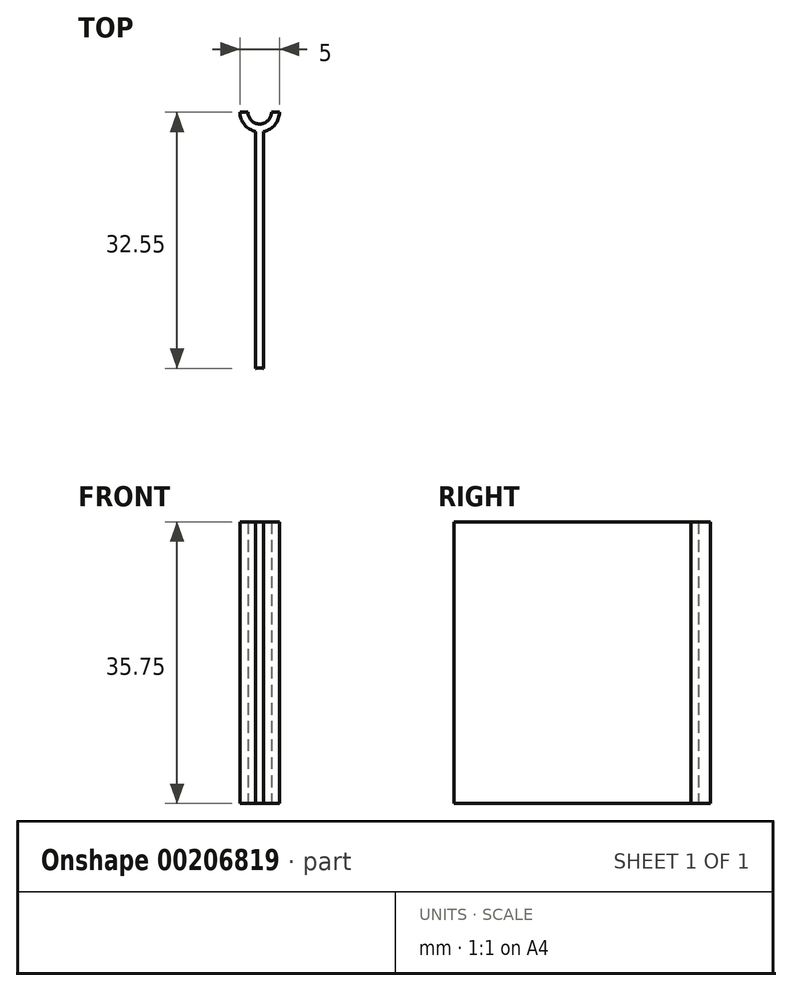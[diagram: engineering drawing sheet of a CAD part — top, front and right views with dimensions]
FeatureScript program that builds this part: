
annotation { "Feature Type Name" : "Feature", "Feature Type Description" : "" }
export const myFeature = defineFeature(function(context is Context, id is Id, definition is map)
    precondition{}
    {
        {
            var Q0;
            Q0=qCreatedBy(makeId("Top.planeOp"),FACE);
            var sketch = newSketch(context, id + "F0", { "sketchPlane" : qUnion([Q0])});
            skLineSegment(sketch, "E0.bottom", {"start": v(2.5, 17.5) * mm, "end": v(-2.5, 17.5) * mm, "construction": true});
            skLineSegment(sketch, "E0.top", {"start": v(2.5, -17.5) * mm, "end": v(-2.5, -17.5) * mm, "construction": true});
            skLineSegment(sketch, "E0.left", {"start": v(2.5, 17.5) * mm, "end": v(2.5, -17.5) * mm, "construction": true});
            skLineSegment(sketch, "E0.right", {"start": v(-2.5, 17.5) * mm, "end": v(-2.5, -17.5) * mm, "construction": true});
            skPoint(sketch, "E0.middle", {"position": v(0, 0) * mm});
            skLineSegment(sketch, "E1", {"start": v(0, 0) * mm, "end": v(0, 17.5) * mm});
            skLineSegment(sketch, "E2", {"start": v(0, 17.5) * mm, "end": v(0, -17.5) * mm, "construction": true});
            skLineSegment(sketch, "E3.left", {"start": v(-0.5, 15.05) * mm, "end": v(-0.5, -15.05) * mm});
            skLineSegment(sketch, "E3.right", {"start": v(0.5, 15.05) * mm, "end": v(0.5, -15.05) * mm});
            skArc(sketch, "E4", {"start": v(-2.5, 17.5) * mm, "mid": v(0, 15) * mm, "end": v(2.5, 17.5) * mm});
            skArc(sketch, "E5", {"start": v(-1.5, 17.5) * mm, "mid": v(0, 16) * mm, "end": v(1.5, 17.5) * mm});
            skLineSegment(sketch, "E6", {"start": v(-2.5, 17.5) * mm, "end": v(-1.5, 17.5) * mm});
            skLineSegment(sketch, "E7", {"start": v(1.5, 17.5) * mm, "end": v(2.5, 17.5) * mm});
            skArc(sketch, "E8", {"start": v(-2.5, -17.5) * mm, "mid": v(0, -15) * mm, "end": v(2.5, -17.5) * mm});
            skArc(sketch, "E9", {"start": v(-1.5, -17.5) * mm, "mid": v(0, -16) * mm, "end": v(1.5, -17.5) * mm});
            skLineSegment(sketch, "E10", {"start": v(-2.5, -17.5) * mm, "end": v(-1.5, -17.5) * mm});
            skLineSegment(sketch, "E11", {"start": v(1.5, -17.5) * mm, "end": v(2.5, -17.5) * mm});
            skSolve(sketch);
        }
        {
            var Q0;
            {var subQ0=sQuery(id+"F0.wireOp",EDGE,"E6");Q0=makeQuery(id+"F0.imprint","IMPRINT",FACE,{"disambiguationData":[TD([[makeQuery(id+"F0.imprint","IMPRINT",EDGE,{"derivedFrom":subQ0}),-1.0]])]});}
            var Q1;
            {var subQ0=sQuery(id+"F0.wireOp",EDGE,"E7");Q1=makeQuery(id+"F0.imprint","IMPRINT",FACE,{"disambiguationData":[TD([[makeQuery(id+"F0.imprint","IMPRINT",EDGE,{"derivedFrom":subQ0}),-1.0]])]});}
            var Q2;
            {var subQ4=sQuery(id+"F0.wireOp",EDGE,"E3.left");Q2=makeQuery(id+"F0.imprint","IMPRINT",FACE,{"disambiguationData":[TD([[makeQuery(id+"F0.imprint","IMPRINT",EDGE,{"derivedFrom":subQ4}),1.0]])]});}
            var Q3;
            {var subQ1=sQuery(id+"F0.wireOp",EDGE,"E3.top");Q3=makeQuery(id+"F0.imprint","IMPRINT",FACE,{"disambiguationData":[TD([[makeQuery(id+"F0.imprint","IMPRINT",EDGE,{"derivedFrom":subQ1}),-1.0]])]});}
            var Q4;
            Q4=makeQuery(id+"F0.imprint","IMPRINT",FACE,{"disambiguationData":[TD([[makeQuery(id+"F0.imprint","IMPRINT",EDGE,{"derivedFrom":sQuery(id+"F0.wireOp",EDGE,"E9")}),1.0]])]});
            extrude(context, id + "F1", {"entities" : qUnion([Q0, Q1, Q2, Q3, Q4]), "depth" : 35.75 * mm});
        }
    });
